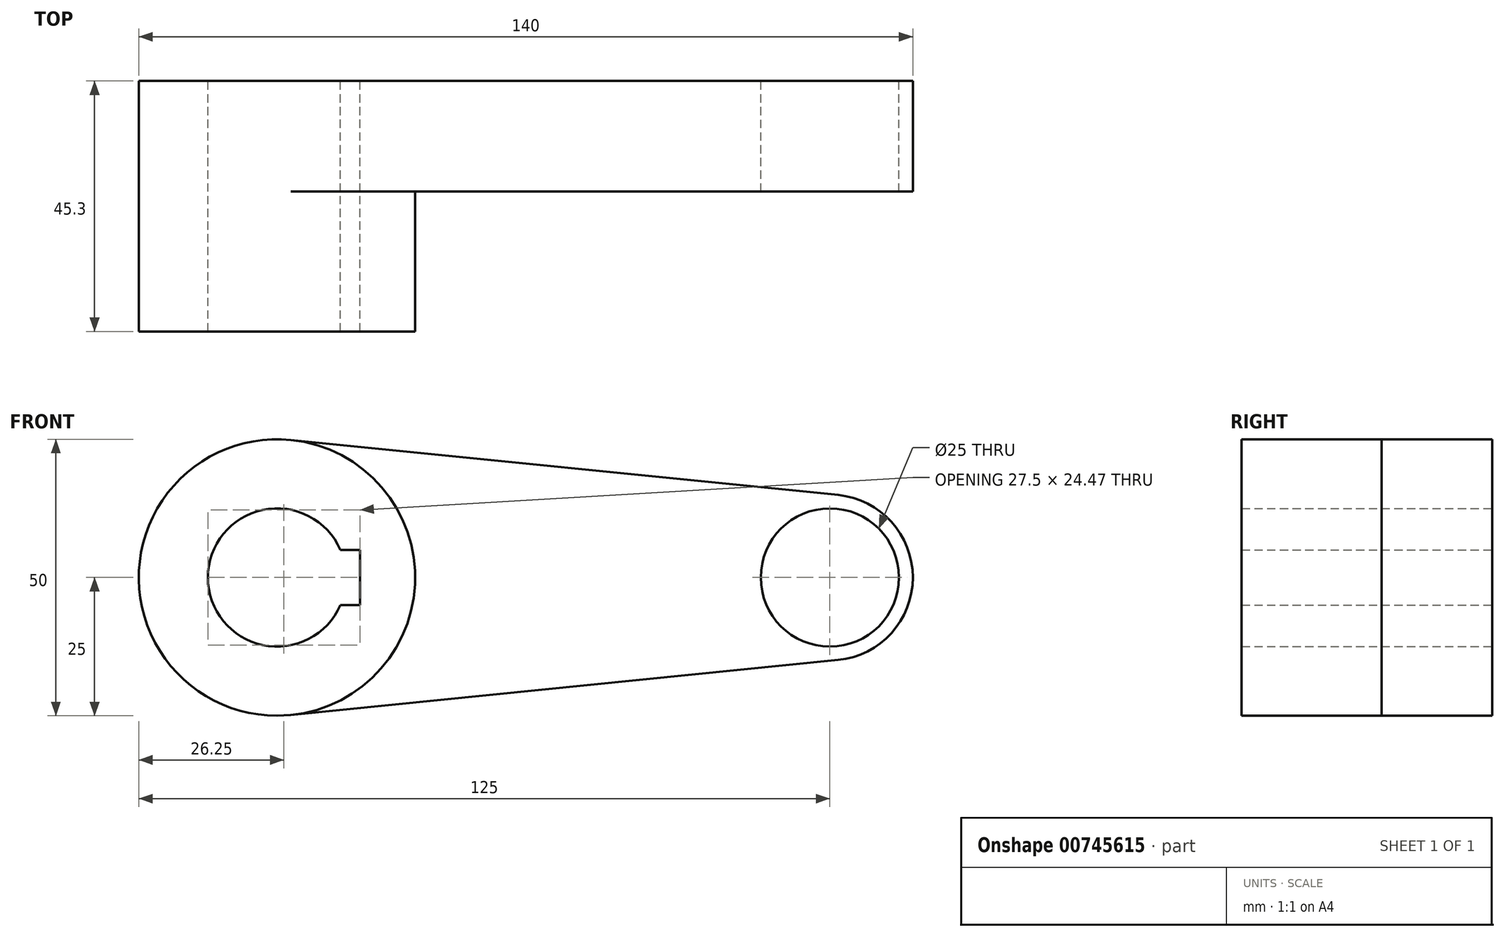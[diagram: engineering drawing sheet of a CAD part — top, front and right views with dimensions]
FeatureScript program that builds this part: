
annotation { "Feature Type Name" : "Feature", "Feature Type Description" : "" }
export const myFeature = defineFeature(function(context is Context, id is Id, definition is map)
    precondition{}
    {
        {
            var Q0;
            Q0=qCreatedBy(makeId("Front.planeOp"),FACE);
            var sketch = newSketch(context, id + "F0", { "sketchPlane" : qUnion([Q0])});
            skCircle(sketch, "E0", {"center": v(0, 0) * mm, "radius": 25 * mm});
            skCircle(sketch, "E1", {"center": v(100, 0) * mm, "radius": 15 * mm});
            skLineSegment(sketch, "E2", {"start": v(2.5, 24.87) * mm, "end": v(101.5, 14.92) * mm});
            skLineSegment(sketch, "E3", {"start": v(2.5, -24.87) * mm, "end": v(101.5, -14.92) * mm});
            skCircle(sketch, "E4", {"center": v(0, 0) * mm, "radius": 12.5 * mm});
            skCircle(sketch, "E5", {"center": v(100, 0) * mm, "radius": 12.5 * mm});
            skLineSegment(sketch, "E6.bottom", {"start": v(15, -5) * mm, "end": v(-15, -5) * mm});
            skLineSegment(sketch, "E6.top", {"start": v(15, 5) * mm, "end": v(-15, 5) * mm});
            skLineSegment(sketch, "E6.left", {"start": v(15, -5) * mm, "end": v(15, 5) * mm});
            skLineSegment(sketch, "E6.right", {"start": v(-15, -5) * mm, "end": v(-15, 5) * mm});
            skSolve(sketch);
        }
        {
            var Q0;
            {var subQ0=sQuery(id+"F0.wireOp",EDGE,"E2");Q0=makeQuery(id+"F0.imprint","IMPRINT",FACE,{"disambiguationData":[TD([[makeQuery(id+"F0.imprint","IMPRINT",EDGE,{"derivedFrom":subQ0}),-1.0]])]});}
            var Q1;
            {var subQ7=sQuery(id+"F0.wireOp",EDGE,"E6.left");Q1=makeQuery(id+"F0.imprint","IMPRINT",FACE,{"disambiguationData":[TD([[makeQuery(id+"F0.imprint","IMPRINT",EDGE,{"derivedFrom":subQ7}),-1.0]])]});}
            var Q2;
            Q2=makeQuery(id+"F0.imprint","IMPRINT",FACE,{"disambiguationData":[TD([[makeQuery(id+"F0.imprint","IMPRINT",EDGE,{"derivedFrom":sQuery(id+"F0.wireOp",EDGE,"E5")}),-1.0]])]});
            var Q3;
            {var subQ5=sQuery(id+"F0.wireOp",EDGE,"E6.right");Q3=makeQuery(id+"F0.imprint","IMPRINT",FACE,{"disambiguationData":[TD([[makeQuery(id+"F0.imprint","IMPRINT",EDGE,{"derivedFrom":subQ5}),-1.0]])]});}
            extrude(context, id + "F1", {"entities" : qUnion([Q0, Q1, Q2, Q3]), "depth" : 20 * mm, "offsetDistance" : 25 * mm});
        }
        {
            var Q0;
            {var subQ7=sQuery(id+"F0.wireOp",EDGE,"E6.left");Q0=makeQuery(id+"F0.imprint","IMPRINT",FACE,{"disambiguationData":[TD([[makeQuery(id+"F0.imprint","IMPRINT",EDGE,{"derivedFrom":subQ7}),-1.0]])]});}
            var Q1;
            {var subQ5=sQuery(id+"F0.wireOp",EDGE,"E6.right");Q1=makeQuery(id+"F0.imprint","IMPRINT",FACE,{"disambiguationData":[TD([[makeQuery(id+"F0.imprint","IMPRINT",EDGE,{"derivedFrom":subQ5}),-1.0]])]});}
            extrude(context, id + "F2", {"entities" : qUnion([Q0, Q1]), "operationType" : NewBodyOperationType.ADD, "depth" : 45.3 * mm, "offsetDistance" : 25 * mm});
        }
    });
